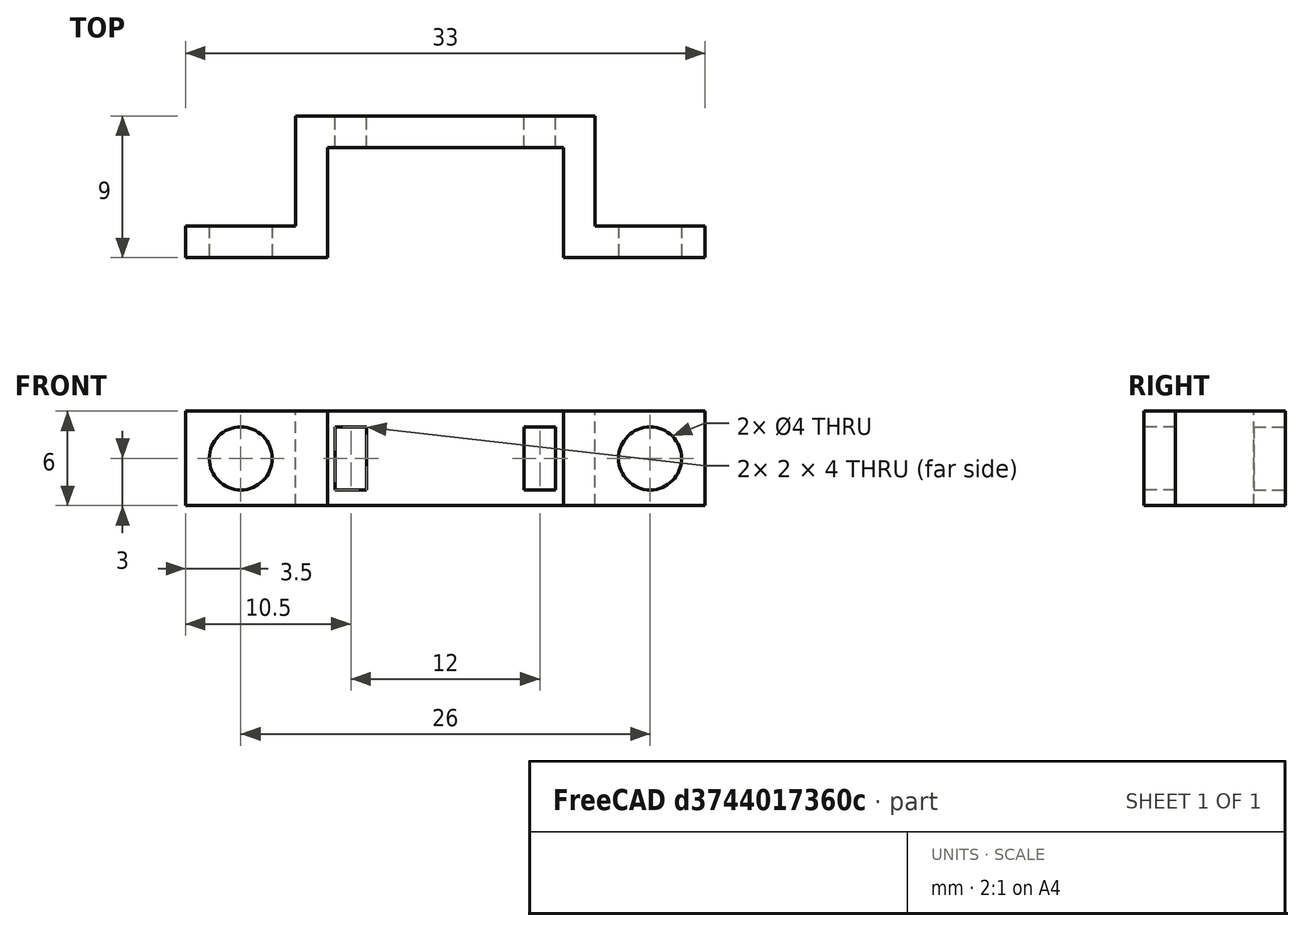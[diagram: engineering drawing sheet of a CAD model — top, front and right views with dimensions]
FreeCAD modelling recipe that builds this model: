
FCSTD DOCUMENT  (FreeCAD 0.18R16161 (Git))
Label: potSupport
License: All rights reserved
LicenseURL: http://en.wikipedia.org/wiki/All_rights_reserved
objects: Part::Box×7, Part::Cut×4, Part::MultiFuse×4, Part::Cylinder×2
note: 17 computed .brp shape members not serialized (recipe doc carries the construction recipe); baked Part::Feature solids carry a one-line shape summary decoded from their .brp

FEATURE [Part::Box] Box  label="Cube"
  AttacherType = Attacher::AttachEngine3D
  Height = 9
  Length = 19
  Width = 2
FEATURE [Part::Box] Box001  label="Cube001"
  AttacherType = Attacher::AttachEngine3D
  Height = 9
  Length = 2
  Placement = pos=(0,-7,0) rot=(0,0,1;0rad)
  Width = 7
FEATURE [Part::Box] Box002  label="Cube002"
  AttacherType = Attacher::AttachEngine3D
  Height = 9
  Length = 2
  Placement = pos=(17,-7,0) rot=(0,0,1;0rad)
  Width = 7
FEATURE [Part::Box] Box003  label="Cube003"
  AttacherType = Attacher::AttachEngine3D
  Height = 9
  Length = 7
  Placement = pos=(-7,-7,0) rot=(0,0,1;0rad)
  Width = 2
FEATURE [Part::Box] Box004  label="Cube004"
  AttacherType = Attacher::AttachEngine3D
  Height = 9
  Length = 7
  Placement = pos=(19,-7,0) rot=(0,0,1;0rad)
  Width = 2
FEATURE [Part::Cylinder] Cylinder
  Angle = 360
  AttacherType = Attacher::AttachEngine3D
  Height = 10
  Placement = pos=(-3.5,0,3) rot=(1,0,0;1.5708rad)
  Radius = 2
FEATURE [Part::Cylinder] Cylinder001
  Angle = 360
  AttacherType = Attacher::AttachEngine3D
  Height = 10
  Placement = pos=(22.5,0,3) rot=(1,0,0;1.5708rad)
  Radius = 2
FEATURE [Part::Cut] Cut
  Base = -> Box003
  Tool = -> Cylinder
FEATURE [Part::Cut] Cut001
  Base = -> Box004
  Tool = -> Cylinder001
FEATURE [Part::Box] Box005  label="Cube005"
  AttacherType = Attacher::AttachEngine3D
  Height = 4
  Length = 2
  Placement = pos=(2.5,-3,1) rot=(0,0,1;0rad)
  Width = 6
FEATURE [Part::Box] Box006  label="Cube006"
  AttacherType = Attacher::AttachEngine3D
  Height = 4
  Length = 2
  Placement = pos=(14.5,-3,1) rot=(0,0,1;0rad)
  Width = 6
FEATURE [Part::Cut] Cut002
  Base = -> Box
  Tool = -> Box005
FEATURE [Part::Cut] Cut003
  Base = -> Cut002
  Tool = -> Box006
FEATURE [Part::MultiFuse] Fusion
  Shapes = -> [Cut,Box001]
FEATURE [Part::MultiFuse] Fusion001
  Shapes = -> [Cut003,Fusion]
FEATURE [Part::MultiFuse] Fusion002
  Shapes = -> [Fusion001,Box002]
FEATURE [Part::MultiFuse] Fusion003
  Shapes = -> [Fusion002,Cut001]
